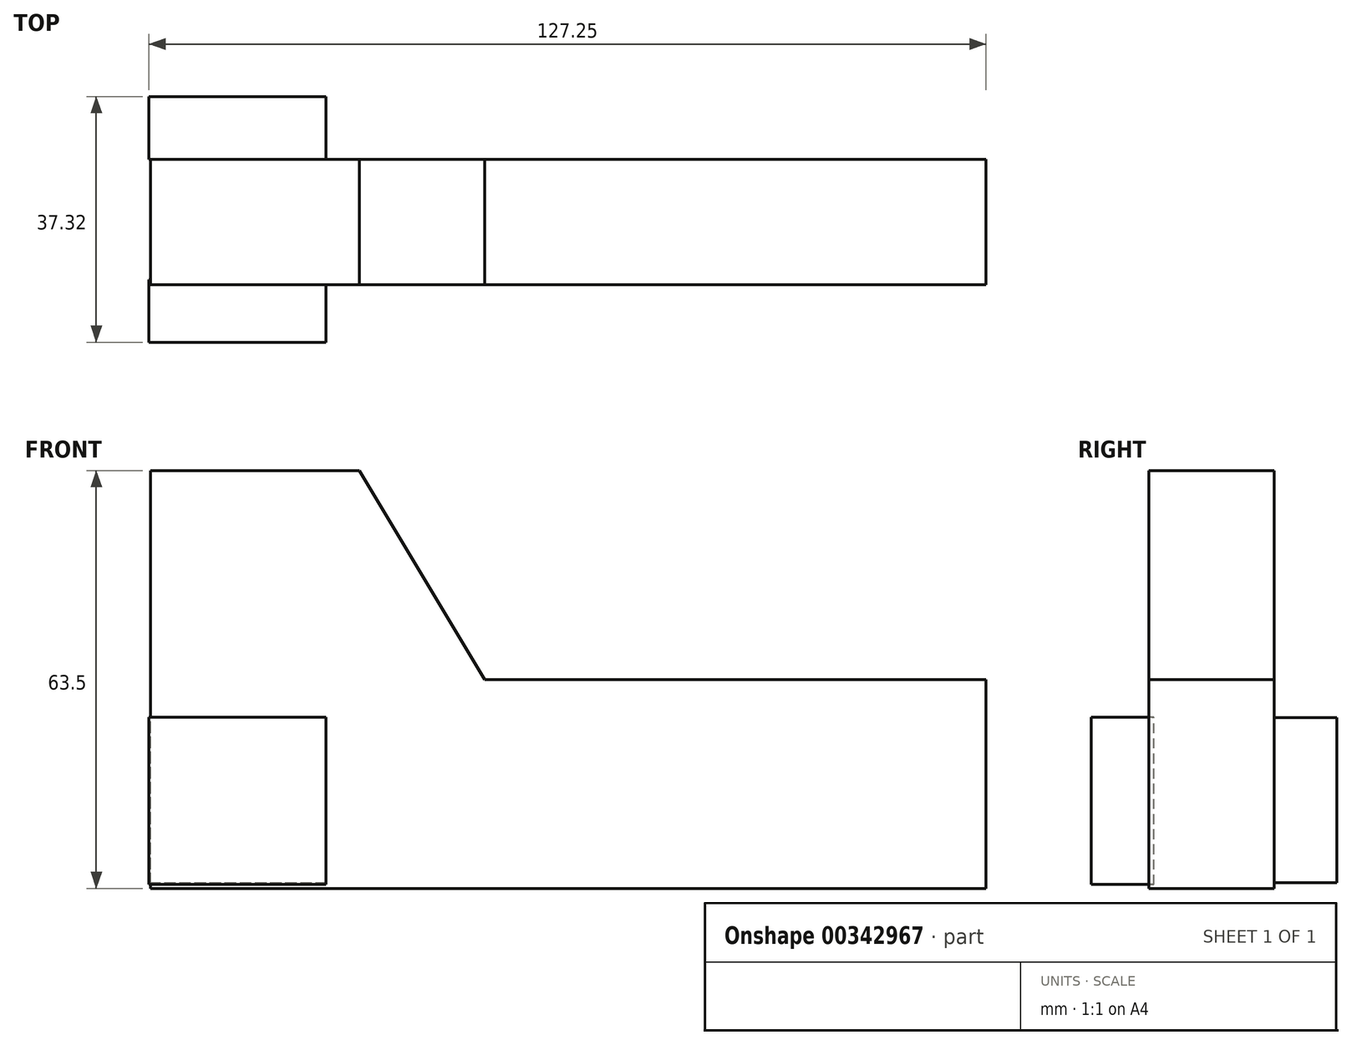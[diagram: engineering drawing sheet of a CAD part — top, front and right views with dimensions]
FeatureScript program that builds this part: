
annotation { "Feature Type Name" : "Feature", "Feature Type Description" : "" }
export const myFeature = defineFeature(function(context is Context, id is Id, definition is map)
    precondition{}
    {
        {
            var Q0;
            Q0=qCreatedBy(makeId("Front.planeOp"),FACE);
            var sketch = newSketch(context, id + "F0", { "sketchPlane" : qUnion([Q0])});
            skLineSegment(sketch, "E0", {"start": v(-71.12, -46.2) * mm, "end": v(55.88, -46.2) * mm});
            skLineSegment(sketch, "E1", {"start": v(-71.12, -46.2) * mm, "end": v(-71.12, 17.3) * mm});
            skLineSegment(sketch, "E2", {"start": v(55.88, -46.2) * mm, "end": v(55.88, -14.45) * mm});
            skLineSegment(sketch, "E3", {"start": v(-71.12, 17.3) * mm, "end": v(-39.37, 17.3) * mm});
            skLineSegment(sketch, "E4", {"start": v(55.88, -14.45) * mm, "end": v(-20.32, -14.45) * mm});
            skLineSegment(sketch, "E5", {"start": v(-39.37, 17.3) * mm, "end": v(-20.32, -14.45) * mm});
            skSolve(sketch);
        }
        {
            var Q0;
            Q0 = qSketchRegion(id + "F0", true);
            extrude(context, id + "F1", {"entities" : qUnion([Q0]), "depth" : 19.05 * mm});
        }
        {
            var Q0;
            Q0=qCreatedBy(makeId("Right.planeOp"),FACE);
            var sketch = newSketch(context, id + "F2", { "sketchPlane" : qUnion([Q0])});
            skLineSegment(sketch, "E6", {"start": v(-18.26, -45.62) * mm, "end": v(-27.79, -45.62) * mm});
            skLineSegment(sketch, "E7", {"start": v(-27.79, -45.62) * mm, "end": v(-27.79, -20.22) * mm});
            skLineSegment(sketch, "E8", {"start": v(-27.79, -20.22) * mm, "end": v(-18.26, -20.22) * mm});
            skLineSegment(sketch, "E9", {"start": v(0, -45.32) * mm, "end": v(9.53, -45.32) * mm});
            skLineSegment(sketch, "E10", {"start": v(0, -20.26) * mm, "end": v(9.53, -20.26) * mm});
            skLineSegment(sketch, "E11", {"start": v(9.53, -20.26) * mm, "end": v(9.53, -45.32) * mm});
            skLineSegment(sketch, "E12", {"start": v(-18.26, -20.22) * mm, "end": v(-18.26, -45.62) * mm});
            skLineSegment(sketch, "E13", {"start": v(0, -20.26) * mm, "end": v(0, -45.32) * mm});
            skSolve(sketch);
        }
        {
            var Q0;
            Q0 = qSketchRegion(id + "F2", true);
            extrude(context, id + "F3", {"entities" : qUnion([Q0]), "operationType" : NewBodyOperationType.ADD, "oppositeDirection" : true, "depth" : 71.37 * mm, "hasSecondDirection" : true, "secondDirectionOppositeDirection" : true, "secondDirectionDepth" : 44.45 * mm});
        }
    });
